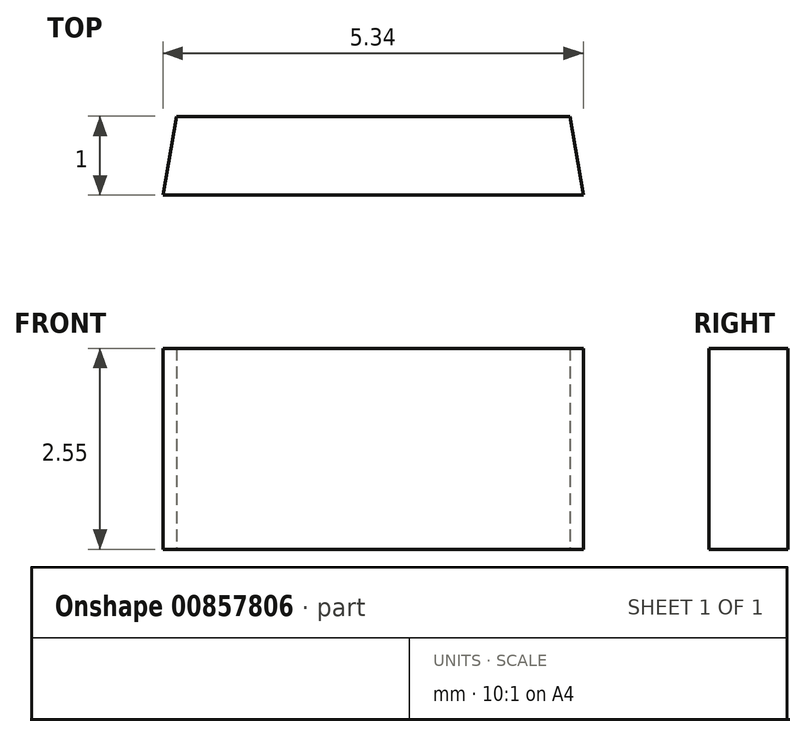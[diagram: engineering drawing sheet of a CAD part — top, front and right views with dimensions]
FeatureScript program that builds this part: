
annotation { "Feature Type Name" : "Feature", "Feature Type Description" : "" }
export const myFeature = defineFeature(function(context is Context, id is Id, definition is map)
    precondition{}
    {
        {
            var Q0;
            Q0=qCreatedBy(makeId("Top.planeOp"),FACE);
            var sketch = newSketch(context, id + "F0", { "sketchPlane" : qUnion([Q0])});
            skLineSegment(sketch, "E0", {"start": v(-3.17, 2.66) * mm, "end": v(1.83, 2.66) * mm});
            skPoint(sketch, "E1", {"position": v(-0.67, 2.66) * mm});
            skLineSegment(sketch, "E2", {"start": v(-3.34, 1.66) * mm, "end": v(2, 1.66) * mm});
            skPoint(sketch, "E3", {"position": v(-0.67, 1.66) * mm});
            skLineSegment(sketch, "E4", {"start": v(-3.17, 2.66) * mm, "end": v(-3.34, 1.66) * mm});
            skLineSegment(sketch, "E5", {"start": v(1.83, 2.66) * mm, "end": v(2, 1.66) * mm});
            skSolve(sketch);
        }
        {
            var Q0;
            Q0 = qSketchRegion(id + "F0", true);
            extrude(context, id + "F1", {"entities" : qUnion([Q0]), "depth" : 2.55 * mm, "offsetDistance" : 25 * mm});
        }
    });
